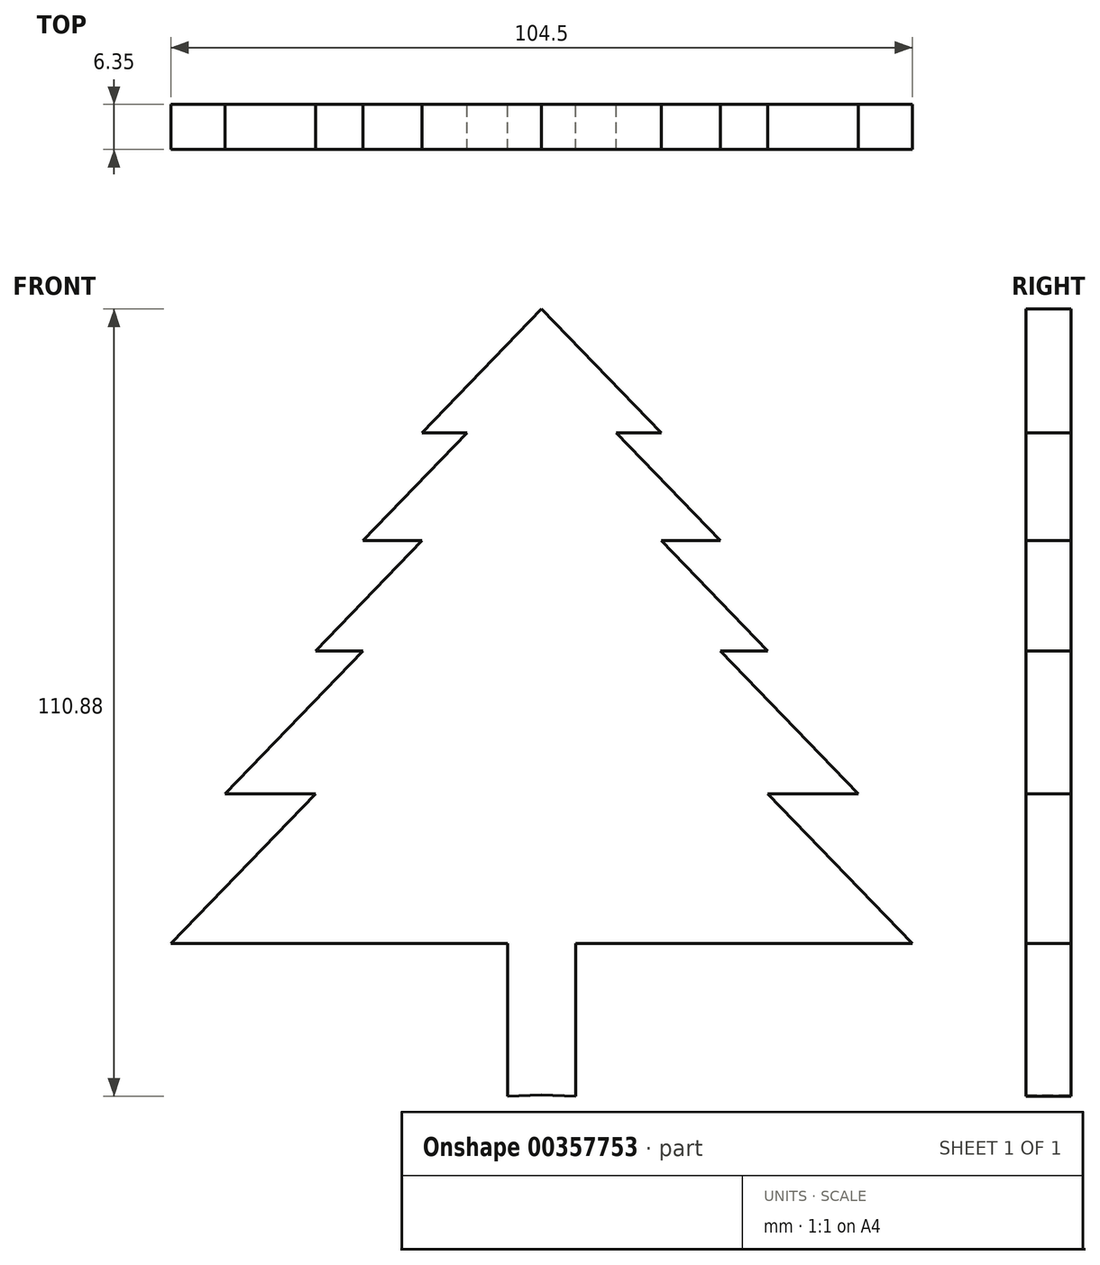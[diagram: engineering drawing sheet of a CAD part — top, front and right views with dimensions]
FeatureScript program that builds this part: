
annotation { "Feature Type Name" : "Feature", "Feature Type Description" : "" }
export const myFeature = defineFeature(function(context is Context, id is Id, definition is map)
    precondition{}
    {
        {
            var Q0;
            Q0=qCreatedBy(makeId("Front.planeOp"),FACE);
            var sketch = newSketch(context, id + "F0", { "sketchPlane" : qUnion([Q0])});
            skLineSegment(sketch, "E0", {"start": v(0, -21.12) * mm, "end": v(0, -42.41) * mm});
            skLineSegment(sketch, "E1", {"start": v(0, 68.28) * mm, "end": v(-16.84, 50.83) * mm});
            skLineSegment(sketch, "E2", {"start": v(-16.84, 50.83) * mm, "end": v(-10.53, 50.83) * mm});
            skLineSegment(sketch, "E3", {"start": v(-10.53, 50.83) * mm, "end": v(-25.17, 35.66) * mm});
            skLineSegment(sketch, "E4", {"start": v(-25.17, 35.66) * mm, "end": v(-16.84, 35.66) * mm});
            skLineSegment(sketch, "E5", {"start": v(-16.84, 35.66) * mm, "end": v(-31.85, 20.12) * mm});
            skLineSegment(sketch, "E6", {"start": v(-31.85, 20.12) * mm, "end": v(-25.17, 20.12) * mm});
            skLineSegment(sketch, "E7", {"start": v(-25.17, 20.12) * mm, "end": v(-44.6, 0) * mm});
            skLineSegment(sketch, "E8", {"start": v(-44.6, 0) * mm, "end": v(-31.85, 0) * mm});
            skLineSegment(sketch, "E9", {"start": v(-31.85, 0) * mm, "end": v(-52.25, -21.12) * mm});
            skLineSegment(sketch, "E10", {"start": v(-52.25, -21.12) * mm, "end": v(-4.81, -21.12) * mm});
            skLineSegment(sketch, "E11", {"start": v(-4.81, -21.12) * mm, "end": v(-4.81, -42.6) * mm});
            skLineSegment(sketch, "E12", {"start": v(-4.81, -42.6) * mm, "end": v(0, -42.41) * mm});
            skPoint(sketch, "E13.orphan", {"position": v(0, -21.12) * mm});
            skLineSegment(sketch, "E14.MirrorCS", {"start": v(0, 68.28) * mm, "end": v(16.84, 50.83) * mm});
            skLineSegment(sketch, "E15.MirrorCS", {"start": v(16.84, 50.83) * mm, "end": v(10.53, 50.83) * mm});
            skLineSegment(sketch, "E16.MirrorCS", {"start": v(10.53, 50.83) * mm, "end": v(25.17, 35.66) * mm});
            skLineSegment(sketch, "E17.MirrorCS", {"start": v(25.17, 35.66) * mm, "end": v(16.84, 35.66) * mm});
            skLineSegment(sketch, "E18.MirrorCS", {"start": v(16.84, 35.66) * mm, "end": v(31.85, 20.12) * mm});
            skLineSegment(sketch, "E19.MirrorCS", {"start": v(31.85, 20.12) * mm, "end": v(25.17, 20.12) * mm});
            skLineSegment(sketch, "E20.MirrorCS", {"start": v(25.17, 20.12) * mm, "end": v(44.6, 0) * mm});
            skLineSegment(sketch, "E21.MirrorCS", {"start": v(44.6, 0) * mm, "end": v(31.85, 0) * mm});
            skLineSegment(sketch, "E22.MirrorCS", {"start": v(31.85, 0) * mm, "end": v(52.25, -21.12) * mm});
            skLineSegment(sketch, "E23.MirrorCS", {"start": v(52.25, -21.12) * mm, "end": v(4.81, -21.12) * mm});
            skLineSegment(sketch, "E24.MirrorCS", {"start": v(4.81, -21.12) * mm, "end": v(4.81, -42.6) * mm});
            skLineSegment(sketch, "E25.MirrorCS", {"start": v(4.81, -42.6) * mm, "end": v(0, -42.41) * mm});
            skSolve(sketch);
        }
        {
            var Q0;
            Q0 = qSketchRegion(id + "F0", true);
            extrude(context, id + "F1", {"entities" : qUnion([Q0]), "depth" : 6.35 * mm});
        }
    });
